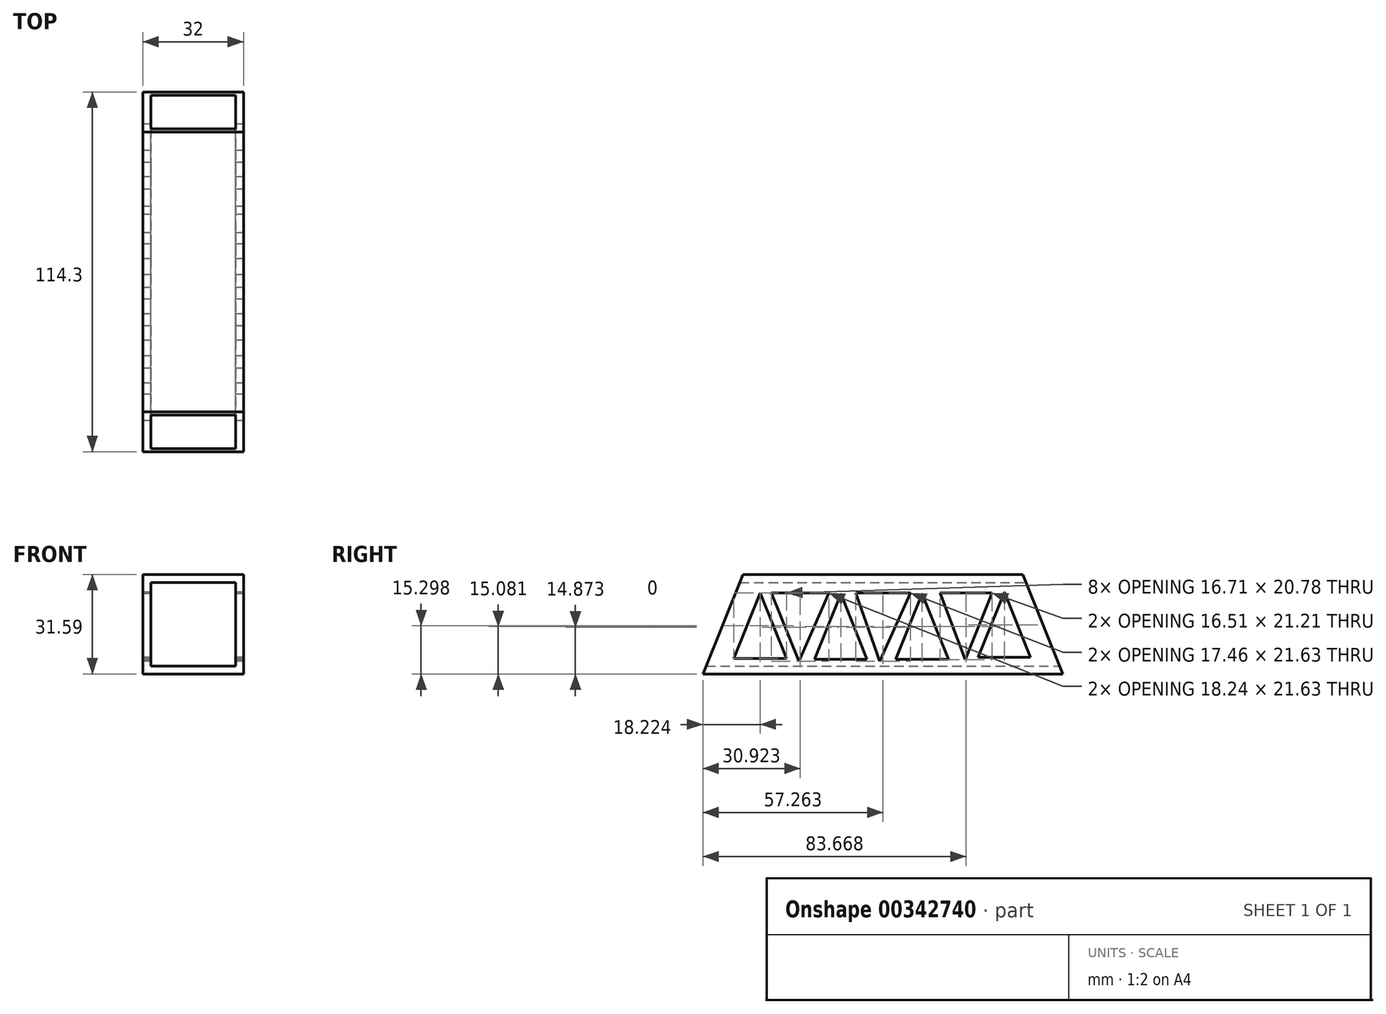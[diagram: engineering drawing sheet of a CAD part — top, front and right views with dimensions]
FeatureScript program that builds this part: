
annotation { "Feature Type Name" : "Feature", "Feature Type Description" : "" }
export const myFeature = defineFeature(function(context is Context, id is Id, definition is map)
    precondition{}
    {
        {
            var Q0;
            Q0=qCreatedBy(makeId("Right.planeOp"),FACE);
            var sketch = newSketch(context, id + "F0", { "sketchPlane" : qUnion([Q0])});
            skLineSegment(sketch, "E0", {"start": v(-62.46, -19.46) * mm, "end": v(-49.76, 12.13) * mm});
            skLineSegment(sketch, "E1", {"start": v(-49.76, 12.13) * mm, "end": v(39.14, 12.13) * mm});
            skLineSegment(sketch, "E2", {"start": v(39.14, 12.13) * mm, "end": v(51.84, -19.46) * mm});
            skLineSegment(sketch, "E3", {"start": v(51.84, -19.46) * mm, "end": v(-62.46, -19.46) * mm});
            skLineSegment(sketch, "E4", {"start": v(-44.24, 6.23) * mm, "end": v(-52.6, -14.55) * mm});
            skLineSegment(sketch, "E5", {"start": v(-52.6, -14.55) * mm, "end": v(-35.88, -14.55) * mm});
            skLineSegment(sketch, "E6", {"start": v(-35.88, -14.55) * mm, "end": v(-44.24, 6.23) * mm});
            skLineSegment(sketch, "E7", {"start": v(-27, -14.76) * mm, "end": v(-18.64, 6.02) * mm});
            skLineSegment(sketch, "E8", {"start": v(-18.64, 6.02) * mm, "end": v(-10.29, -14.76) * mm});
            skLineSegment(sketch, "E9", {"start": v(-27, -14.76) * mm, "end": v(-10.29, -14.76) * mm});
            skLineSegment(sketch, "E10", {"start": v(-1.18, -14.76) * mm, "end": v(7.18, 6.02) * mm});
            skLineSegment(sketch, "E11", {"start": v(7.18, 6.02) * mm, "end": v(15.53, -14.76) * mm});
            skLineSegment(sketch, "E12", {"start": v(15.53, -14.76) * mm, "end": v(-1.18, -14.76) * mm});
            skLineSegment(sketch, "E13", {"start": v(24.94, -14.23) * mm, "end": v(33.3, 6.55) * mm});
            skLineSegment(sketch, "E14", {"start": v(33.3, 6.55) * mm, "end": v(41.65, -14.23) * mm});
            skLineSegment(sketch, "E15", {"start": v(41.65, -14.23) * mm, "end": v(24.94, -14.23) * mm});
            skLineSegment(sketch, "E16", {"start": v(-40.66, 6.23) * mm, "end": v(-22.42, 6.23) * mm});
            skLineSegment(sketch, "E17", {"start": v(-22.42, 6.23) * mm, "end": v(-31.96, -15.4) * mm});
            skLineSegment(sketch, "E18", {"start": v(-31.96, -15.4) * mm, "end": v(-40.66, 6.23) * mm});
            skLineSegment(sketch, "E19", {"start": v(-13.93, 6.23) * mm, "end": v(3.54, 6.23) * mm});
            skLineSegment(sketch, "E20", {"start": v(3.54, 6.23) * mm, "end": v(-6.26, -15.4) * mm});
            skLineSegment(sketch, "E21", {"start": v(-6.26, -15.4) * mm, "end": v(-13.93, 6.23) * mm});
            skLineSegment(sketch, "E22", {"start": v(12.95, 6.23) * mm, "end": v(29.46, 6.23) * mm});
            skLineSegment(sketch, "E23", {"start": v(29.46, 6.23) * mm, "end": v(20.93, -14.98) * mm});
            skLineSegment(sketch, "E24", {"start": v(20.93, -14.98) * mm, "end": v(12.95, 6.23) * mm});
            skSolve(sketch);
        }
        {
            var Q0;
            Q0=makeQuery(id+"F0.imprint","IMPRINT",FACE,{"disambiguationData":[TD([[makeQuery(id+"F0.imprint","IMPRINT",EDGE,{"derivedFrom":sQuery(id+"F0.wireOp",EDGE,"E0")}),-1.0]])]});
            extrude(context, id + "F1", {"entities" : qUnion([Q0]), "endBound" : BoundingType.SYMMETRIC, "depth" : 32 * mm});
        }
        {
            var Q0;
            Q0=qCreatedBy(makeId("Front.planeOp"),FACE);
            var sketch = newSketch(context, id + "F2", { "sketchPlane" : qUnion([Q0])});
            skLineSegment(sketch, "E25", {"start": v(-13.46, 9.59) * mm, "end": v(-13.46, -16.92) * mm});
            skLineSegment(sketch, "E26", {"start": v(-13.46, -16.92) * mm, "end": v(13.46, -16.92) * mm});
            skLineSegment(sketch, "E27", {"start": v(13.46, -16.92) * mm, "end": v(13.46, 9.59) * mm});
            skLineSegment(sketch, "E28", {"start": v(13.46, 9.59) * mm, "end": v(-13.46, 9.59) * mm});
            skSolve(sketch);
        }
        {
            var Q0;
            Q0=makeQuery(id+"F2.imprint","IMPRINT",FACE,{"disambiguationData":[TD([[makeQuery(id+"F2.imprint","IMPRINT",EDGE,{"derivedFrom":sQuery(id+"F2.wireOp",EDGE,"E25")}),1.0]])]});
            extrude(context, id + "F3", {"entities" : qUnion([Q0]), "operationType" : NewBodyOperationType.REMOVE, "endBound" : BoundingType.SYMMETRIC, "depth" : 148.34 * mm});
        }
    });
